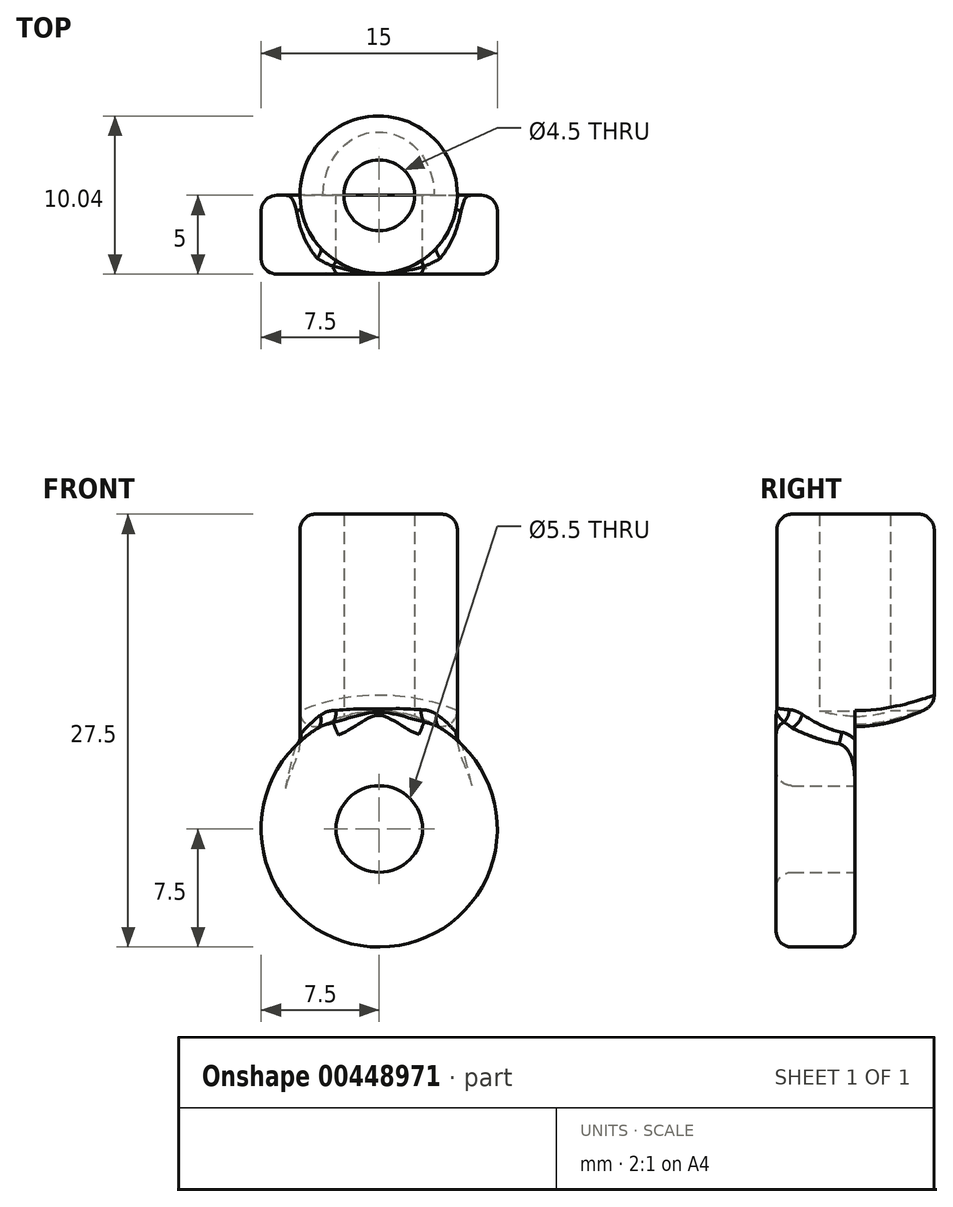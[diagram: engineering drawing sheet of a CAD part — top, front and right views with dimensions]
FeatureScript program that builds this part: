
annotation { "Feature Type Name" : "Feature", "Feature Type Description" : "" }
export const myFeature = defineFeature(function(context is Context, id is Id, definition is map)
    precondition{}
    {
        {
            var Q0;
            Q0=qCreatedBy(makeId("Top.planeOp"),FACE);
            var sketch = newSketch(context, id + "F0", { "sketchPlane" : qUnion([Q0])});
            skCircle(sketch, "E0", {"center": v(-0.04, 0.04) * mm, "radius": 5 * mm});
            skCircle(sketch, "E1", {"center": v(0, 0) * mm, "radius": 2.25 * mm});
            skSolve(sketch);
        }
        {
            var Q0;
            Q0=makeQuery(id+"F0.imprint","IMPRINT",FACE,{"disambiguationData":[TD([[makeQuery(id+"F0.imprint","IMPRINT",EDGE,{"derivedFrom":sQuery(id+"F0.wireOp",EDGE,"E0")}),1.0]])]});
            extrude(context, id + "F1", {"entities" : qUnion([Q0]), "depth" : 20 * mm});
        }
        {
            var Q0;
            Q0=qCreatedBy(makeId("Front.planeOp"),FACE);
            var sketch = newSketch(context, id + "F2", { "sketchPlane" : qUnion([Q0])});
            skCircle(sketch, "E2", {"center": v(0, 0) * mm, "radius": 7.5 * mm});
            skCircle(sketch, "E3", {"center": v(0, 0) * mm, "radius": 2.75 * mm});
            skSolve(sketch);
        }
        {
            var Q0;
            Q0=qSketchRegion(id+"F2",true);
            extrude(context, id + "F3", {"entities" : qUnion([Q0]), "operationType" : NewBodyOperationType.ADD, "depth" : 5 * mm});
        }
        {
            var Q0;
            Q0=qSketchRegion(id+"F2",true);
            var Q1;
            {var subQ1=sQuery(id+"F0.wireOp",EDGE,"E0");var subQ2=sQuery(id+"F2.wireOp",EDGE,"E2");Q1=makeQuery(id+"F3.boolean.opBoolean","SPLIT",FACE,{"disambiguationData":[TD([makeQuery(id+"F3.opExtrude","SWEPT_FACE",FACE,{"disambiguationData":[OSD([subQ2])]})])],"derivedFrom":makeQuery(id+"F1.opExtrude","SWEPT_FACE",FACE,{"disambiguationData":[OSD([subQ1])]})});}
            extrude(context, id + "F4", {"entities" : qUnion([Q0]), "operationType" : NewBodyOperationType.REMOVE, "endBound" : BoundingType.THROUGH_ALL, "oppositeDirection" : true, "endBoundEntityFace" : qUnion([Q1]), "depth" : 25 * mm});
        }
        {
            var Q0;
            Q0=makeQuery(id+"F2.imprint","IMPRINT",FACE,{"disambiguationData":[TD([[makeQuery(id+"F2.imprint","IMPRINT",EDGE,{"derivedFrom":sQuery(id+"F2.wireOp",EDGE,"E3")}),1.0]])]});
            extrude(context, id + "F5", {"entities" : qUnion([Q0]), "operationType" : NewBodyOperationType.REMOVE, "oppositeDirection" : true, "depth" : 25 * mm, "hasSecondDirection" : true, "secondDirectionOppositeDirection" : false, "secondDirectionDepth" : 25 * mm});
        }
        {
            var Q0;
            Q0=makeQuery(id+"F3.opExtrude","CAP_EDGE",EDGE,{"disambiguationData":[OSD([sQuery(id+"F2.wireOp",EDGE,"E2")])],"isStart":false});
            var Q1;
            Q1=makeQuery(id+"F3.opExtrude","CAP_FACE",FACE,{"disambiguationData":[OSD([sQuery(id+"F2.wireOp",EDGE,"E2"),sQuery(id+"F2.wireOp",EDGE,"E3")])],"isStart":false});
            var Q2;
            {var subQ0=sQuery(id+"F2.wireOp",EDGE,"E2");Q2=makeQuery(id+"F3.boolean.opBoolean","SPLIT",EDGE,{"disambiguationData":[TD([makeQuery(id+"F1.opExtrude","SWEPT_FACE",FACE,{"disambiguationData":[OSD([sQuery(id+"F0.wireOp",EDGE,"E0")])]})])],"derivedFrom":makeQuery(id+"F3.opExtrude","CAP_EDGE",EDGE,{"disambiguationData":[OSD([subQ0])],"isStart":true})});}
            fillet(context, id + "F6", {"entities" : qUnion([Q0, Q1, Q2]), "radius" : 1 * mm, "tangentPropagation" : true, "allowEdgeOverflow" : false});
        }
        {
            var Q0;
            Q0=makeQuery(id+"F3.boolean.opBoolean","INTERSECT",EDGE,{"derivedFrom":[makeQuery(id+"F1.opExtrude","SWEPT_FACE",FACE,{"disambiguationData":[OSD([sQuery(id+"F0.wireOp",EDGE,"E0")])]}),makeQuery(id+"F3.opExtrude","SWEPT_FACE",FACE,{"disambiguationData":[OSD([sQuery(id+"F2.wireOp",EDGE,"E2")])]})]});
            var Q1;
            {var subQ0=sQuery(id+"F2.wireOp",EDGE,"E2");var subQ4=sQuery(id+"F0.wireOp",EDGE,"E0");var subQ6=makeQuery(id+"F3.opExtrude","SWEPT_FACE",FACE,{"disambiguationData":[OSD([subQ0])]});Q1=makeQuery(id+"F6.opFillet","BLEND_EDGE",EDGE,{"blendedFrom":[makeQuery(id+"F3.opExtrude","CAP_EDGE",EDGE,{"disambiguationData":[OSD([subQ0])],"isStart":false}),makeQuery(id+"F4.boolean.opBoolean","SPLIT",FACE,{"disambiguationData":[TD([subQ6])],"derivedFrom":makeQuery(id+"F3.boolean.opBoolean","SPLIT",FACE,{"disambiguationData":[TD([subQ6])],"derivedFrom":makeQuery(id+"F1.opExtrude","SWEPT_FACE",FACE,{"disambiguationData":[OSD([subQ4])]})})})],"blendedInto":[makeQuery(id+"F4.boolean.opBoolean","SPLIT",FACE,{"disambiguationData":[TD([subQ6])],"derivedFrom":makeQuery(id+"F3.boolean.opBoolean","SPLIT",FACE,{"disambiguationData":[TD([subQ6])],"derivedFrom":makeQuery(id+"F1.opExtrude","SWEPT_FACE",FACE,{"disambiguationData":[OSD([subQ4])]})})})]});}
            fillet(context, id + "F7", {"entities" : qUnion([Q0, Q1]), "radius" : 1 * mm, "tangentPropagation" : true, "allowEdgeOverflow" : false});
        }
        {
            var Q0;
            {var subQ0=sQuery(id+"F2.wireOp",EDGE,"E2");var subQ2=sQuery(id+"F0.wireOp",EDGE,"E0");Q0=makeQuery(id+"F4.boolean.opBoolean","INTERSECT",EDGE,{"derivedFrom":[makeQuery(id+"F3.boolean.opBoolean","SPLIT",FACE,{"disambiguationData":[TD([makeQuery(id+"F3.opExtrude","SWEPT_FACE",FACE,{"disambiguationData":[OSD([subQ0])]})])],"derivedFrom":makeQuery(id+"F1.opExtrude","SWEPT_FACE",FACE,{"disambiguationData":[OSD([subQ2])]})}),makeQuery(id+"F4.opExtrude","SWEPT_FACE",FACE,{"disambiguationData":[OSD([subQ0])]})]});}
            var Q1;
            Q1=makeQuery(id+"F1.opExtrude","CAP_EDGE",EDGE,{"disambiguationData":[OSD([sQuery(id+"F0.wireOp",EDGE,"E0")])],"isStart":false});
            fillet(context, id + "F8", {"entities" : qUnion([Q0, Q1]), "radius" : 1 * mm, "tangentPropagation" : true, "allowEdgeOverflow" : false});
        }
    });
